# Revit family: Hand_Shower-American_Standard-Three_Function_Shower_Kit-1662.600
name_source: partatom
category: Plumbing Fixtures
revit_build: Autodesk Revit 2014 (Build: 20130308_1515(x64)
units: mm (PartAtom-declared; Revit-internal decimal feet)

## types (1)
- 1662.600
    Assembly Code = D2010710
    CW Connection = Yes
    CWFU = 1
    Cold Water Connection Diameter = 1/2"
    Cold Water Connection Radius = 1/4"
    Default Elevation = 72"
    Description = Complete 3-Function Hand Shower System Kit
    Flow Rate = 1.5 gpm/5.7 lpm
    HW Connection = Yes
    HWFU = 2
    Height = 23 5/8"
    Hot Water Connection Diameter = 1"
    Hot Water Connection Radius = 1/4"
    Installation Type = Wall-Mounted
    Manufacturer = American Standard
    Material = Metal-American Standard-002-Chrome Plated
    Model = 1662.600
    Price = Prices may vary. Please consult Manufacturer Representative for most up-to-date price list.
    Product Documentation Link = https://www.americanstandard-us.com
    Product Page URL = https://www.americanstandard-us.com
    URL = https://www.americanstandard-us.com
    Vent Connection = No
    WFU = 2
    Warranty Information = Limited 1-Year Warranty
    Waste Connection = No
    Width = 5"

## geometry (parser evidence)
native form markers: Sweep x2
no freeform markers — native parametric forms only
